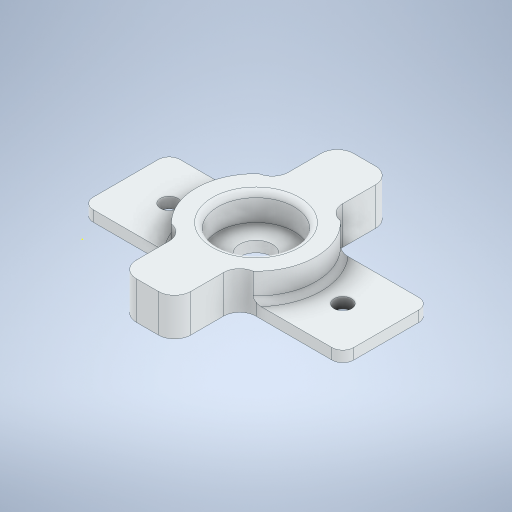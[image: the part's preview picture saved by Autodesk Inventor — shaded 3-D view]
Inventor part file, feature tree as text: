
AUTODESK INVENTOR PART (.ipt)
format: ipt  version: 2024 (Build 280153000, 153)  size: 713,728 bytes
history: native  units: in
note: dims shown in document units (in); Inventor stores cm internally (conversion verified against a paired STEP export)
features: sketch x26, extrude x25, projected_geometry x15, fillet x5
ambient origin geometry x8: Origin, YZ Plane, XZ Plane, XY Plane, X Axis, Y Axis, Z Axis, Center Point
bodies: Solid1 (feature_tree)
feature tree (71):
  sketch  "Sketch1"  dims[d0=47.6875in d1=0.0in d2=1.5in]
  extrude  "Extrusion1"  Depth=1.5in
  extrude  "Extrusion2"  Depth=0.344in
  extrude  "Extrusion3"  Depth=0.344in
  extrude  "Extrusion4"  Depth=0.17in
  extrude  "Extrusion5"  Depth=0.3594in TaperAngle=0.0deg
  extrude  "Extrusion6"  Depth=0.125in
  extrude  "Extrusion7"  Depth=1.0781in TaperAngle=0.0deg
  extrude  "Extrusion8"  Depth=0.125in
  sketch  "Sketch13"  dims[d33=1.0in d34=2.7031in d35=0.0in]
  extrude  "Extrusion9"  Depth=1.3594in TaperAngle=0.0deg
  extrude  "Extrusion10"  Depth=2.7031in TaperAngle=0.0deg
  extrude  "Extrusion11"  Depth=0.1094in TaperAngle=0.0deg
  extrude  "Extrusion12"  Depth=0.75in TaperAngle=0.0deg
  fillet  "Fillet3"  Radius=0.1875in
  extrude  "Extrusion13"  Depth=0.375in
  extrude  "Extrusion14"  Depth=0.951in
  extrude  "Extrusion15"  Depth=1.4375in TaperAngle=0.0deg
  extrude  "Extrusion16"  Depth=0.5in TaperAngle=0.0deg
  sketch  "Sketch22"  dims[d66=1.25in d81=0.2188in d82=0.0in d83=0.0625in]
  extrude  "Extrusion17"  Depth=0.125in TaperAngle=0.0deg
  extrude  "Extrusion18"  Depth=0.875in
  extrude  "Extrusion24"  Depth=0.0625in TaperAngle=0.0deg
  fillet  "Fillet4"  Radius=0.0625in
  extrude  "Extrusion25"  Depth=1.44in TaperAngle=0.0deg
  extrude  "Extrusion26"  Depth=0.0625in TaperAngle=0.0deg
  extrude  "Extrusion27"  Depth=0.5625in TaperAngle=0.0deg
  extrude  "Extrusion28"  Depth=0.0625in
  fillet  "Fillet5"  [1 undecoded]
  extrude  "Extrusion29"  [1 undecoded]
  extrude  "Extrusion30"  [1 undecoded]
  fillet  "Fillet6"  [1 undecoded]
  sketch  "Sketch2"  dims[d3=0.375in d4=0.344in]
  sketch  "Sketch3"  dims[d5=6.4375in d6=0.0in d7=0.344in]
  sketch  "Sketch5"  dims[d8=0.17in d9=0.17in]
  sketch  "Sketch7"  dims[d10=0.3594in d11=0.0in d12=0.3594in d13=0.0in]
  projected_geometry  "Projected Loop1"
  sketch  "Sketch8"  dims[d14=0.1249in d15=0.125in]
  sketch  "Sketch9"  dims[d16=1.0in d17=1.0781in d18=0.0in]
  sketch  "Sketch10"  dims[d19=1.103in d28=0.125in]
  projected_geometry  "Projected Loop2"
  sketch  "Sketch12"  dims[d29=1.0781in d30=0.0in d31=1.3594in d32=0.0in]
  sketch  "Sketch14"  dims[d36=0.9844in d37=0.0in d38=0.1094in d39=0.0in]
  projected_geometry  "Projected Loop4"
  sketch  "Sketch15"  dims[d41=0.75in d42=0.0in d43=0.75in d44=0.0in d45=0.1875in]
  projected_geometry  "Projected Loop5"
  sketch  "Sketch16"  dims[d46=0.375in d47=0.375in]
  sketch  "Sketch17"  dims[d48=0.9511in d49=0.951in]
  sketch  "Sketch18"  dims[d50=0.1875in d51=0.0in d52=1.4375in d53=0.0in]
  sketch  "Sketch19"  dims[d54=0.875in d55=0.0in d56=0.5in d57=0.0in]
  projected_geometry  "Projected Loop6"
  sketch  "Sketch20"  dims[d58=0.375in d59=0.125in d60=0.0in]
  projected_geometry  "Projected Loop7"
  sketch  "Sketch21"  dims[d61=0.125in d62=0.0in d63=0.875in]
  projected_geometry  "Projected Loop8"
  sketch  "Sketch23"  dims[d84=0.185in d85=0.0in d86=1.44in d87=0.0in]
  sketch  "Sketch29"  dims[d88=0.0625in d89=0.0in d90=0.0625in d91=0.0in]
  projected_geometry  "Projected Loop14"
  projected_geometry  "Projected Loop15"
  projected_geometry  "Projected Loop16"
  sketch  "Sketch30"  dims[d92=0.125in d93=0.5625in d94=0.0in]
  projected_geometry  "Projected Loop17"
  sketch  "Sketch31"  dims[d95=0.5625in d96=0.0in d97=0.0625in]
  projected_geometry  "Projected Loop18"
  sketch  "Sketch32"
  projected_geometry  "Projected Loop19"
  sketch  "Sketch33"
  projected_geometry  "Projected Loop20"
  sketch  "Sketch34"
  projected_geometry  "Projected Loop21"
  fillet  "Fillet2"  [1 undecoded]
note: 5 required parameter values undecoded (feature->parameter linkage not recoverable at this tier; creation-order binding heuristic only, values carry confidence <= 0.55)
